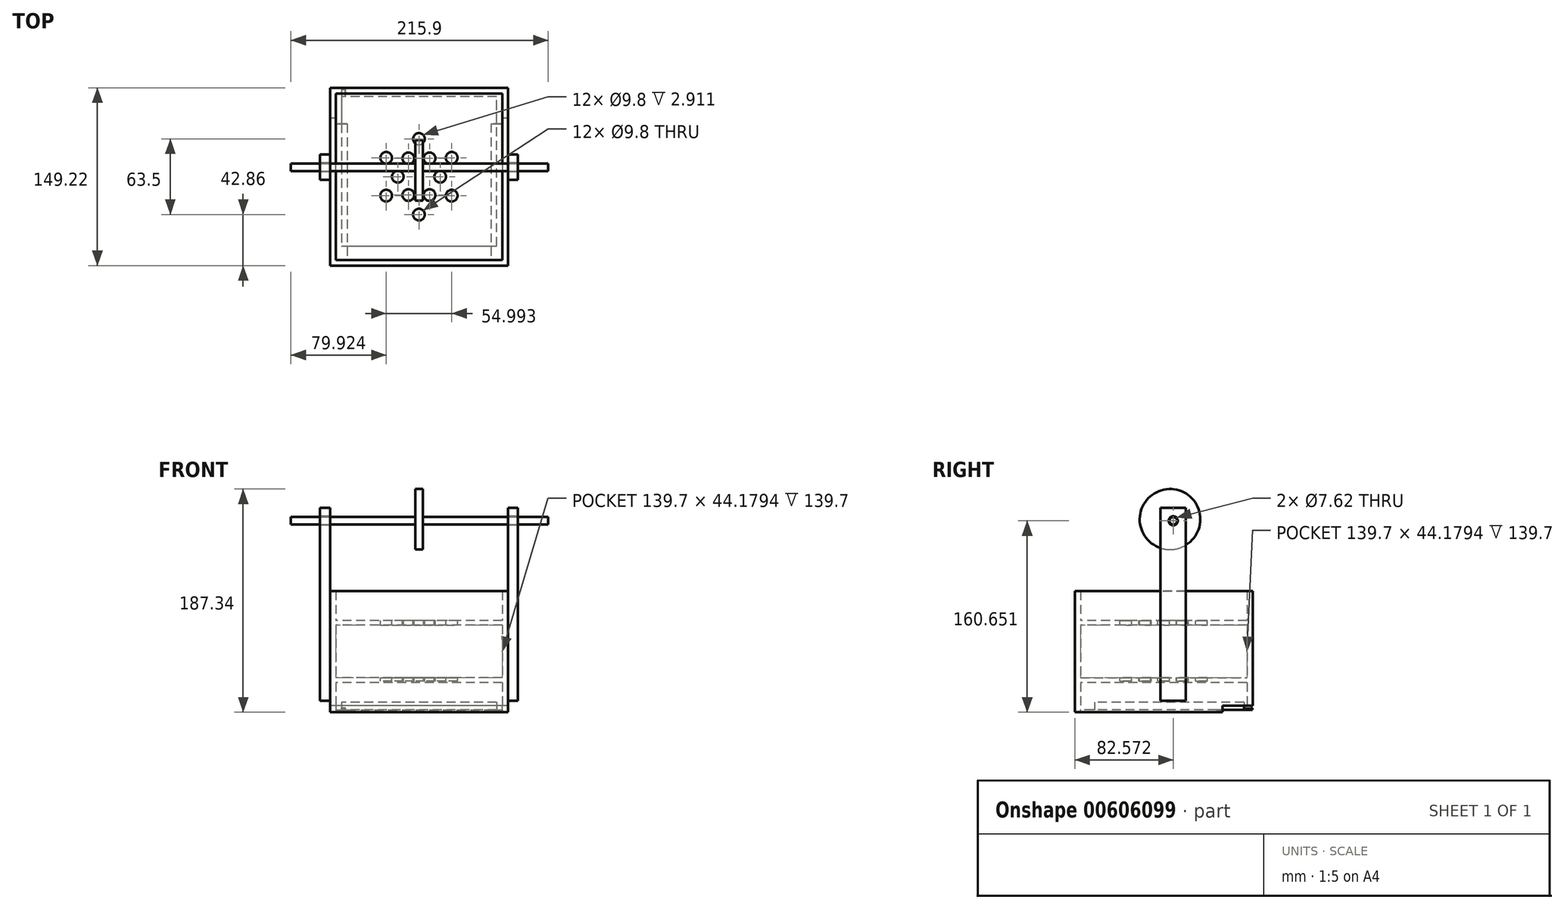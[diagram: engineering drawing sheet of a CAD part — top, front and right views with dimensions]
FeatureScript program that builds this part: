
annotation { "Feature Type Name" : "Feature", "Feature Type Description" : "" }
export const myFeature = defineFeature(function(context is Context, id is Id, definition is map)
    precondition{}
    {
        {
            var Q0;
            Q0=qCreatedBy(makeId("Top.planeOp"),FACE);
            var sketch = newSketch(context, id + "F0", { "sketchPlane" : qUnion([Q0])});
            skLineSegment(sketch, "E0", {"start": v(0, 139.7) * mm, "end": v(139.7, 139.7) * mm});
            skLineSegment(sketch, "E1", {"start": v(139.7, 139.7) * mm, "end": v(139.7, 0) * mm});
            skLineSegment(sketch, "E2", {"start": v(139.7, 0) * mm, "end": v(0, 0) * mm});
            skLineSegment(sketch, "E3", {"start": v(0, 0) * mm, "end": v(0, 139.7) * mm});
            skLineSegment(sketch, "E4", {"start": v(139.7, 95.25) * mm, "end": v(139.7, 69.85) * mm});
            skLineSegment(sketch, "E5", {"start": v(120.65, 19.05) * mm, "end": v(120.65, 120.65) * mm});
            skLineSegment(sketch, "E6", {"start": v(120.65, 120.65) * mm, "end": v(19.05, 120.65) * mm});
            skLineSegment(sketch, "E7", {"start": v(19.05, 120.65) * mm, "end": v(19.05, 19.05) * mm});
            skLineSegment(sketch, "E8", {"start": v(19.05, 19.05) * mm, "end": v(120.65, 19.05) * mm});
            skCircle(sketch, "E9", {"center": v(70, 69.85) * mm, "radius": 45.29 * mm});
            skLineSegment(sketch, "E10", {"start": v(-4.76, 139.7) * mm, "end": v(-4.76, 0) * mm});
            skLineSegment(sketch, "E11", {"start": v(140.6, -4.76) * mm, "end": v(0, -4.76) * mm});
            skLineSegment(sketch, "E12", {"start": v(0, -4.76) * mm, "end": v(-4.76, -4.76) * mm});
            skLineSegment(sketch, "E13", {"start": v(-4.76, -4.76) * mm, "end": v(-4.76, 0) * mm});
            skLineSegment(sketch, "E14", {"start": v(140.6, 144.46) * mm, "end": v(-4.76, 144.46) * mm});
            skLineSegment(sketch, "E15", {"start": v(-4.76, 144.46) * mm, "end": v(-4.76, 139.7) * mm});
            skLineSegment(sketch, "E16", {"start": v(140.6, -4.76) * mm, "end": v(144.46, -4.76) * mm});
            skLineSegment(sketch, "E17", {"start": v(144.46, -4.76) * mm, "end": v(144.46, 144.46) * mm});
            skLineSegment(sketch, "E18", {"start": v(144.46, 144.46) * mm, "end": v(140.6, 144.46) * mm});
            skLineSegment(sketch, "E19", {"start": v(-4.76, 88.47) * mm, "end": v(-13.23, 88.47) * mm});
            skLineSegment(sketch, "E20", {"start": v(-13.23, 88.47) * mm, "end": v(-13.23, 67.15) * mm});
            skLineSegment(sketch, "E21", {"start": v(-13.23, 67.15) * mm, "end": v(-4.76, 67.15) * mm});
            skLineSegment(sketch, "E22", {"start": v(144.46, 88.47) * mm, "end": v(152.93, 88.47) * mm});
            skLineSegment(sketch, "E23", {"start": v(152.93, 88.47) * mm, "end": v(152.93, 73.37) * mm});
            skLineSegment(sketch, "E24", {"start": v(152.93, 73.37) * mm, "end": v(152.93, 67.15) * mm});
            skLineSegment(sketch, "E25", {"start": v(152.93, 67.15) * mm, "end": v(144.46, 67.15) * mm});
            skSolve(sketch);
        }
        {
            var Q0;
            {var subQ1=sQuery(id+"F0.wireOp",EDGE,"E0");Q0=makeQuery(id+"F0.imprint","IMPRINT",FACE,{"disambiguationData":[TD([[makeQuery(id+"F0.imprint","IMPRINT",EDGE,{"derivedFrom":subQ1}),1.0]])]});}
            extrude(context, id + "F1", {"entities" : qUnion([Q0]), "depth" : 101.6 * mm, "offsetDistance" : 25.4 * mm});
        }
        {
            var Q0;
            {var subQ0=sQuery(id+"F0.wireOp",EDGE,"E22");Q0=makeQuery(id+"F0.imprint","IMPRINT",FACE,{"disambiguationData":[TD([[makeQuery(id+"F0.imprint","IMPRINT",EDGE,{"derivedFrom":subQ0}),-1.0]])]});}
            var Q1;
            {var subQ0=sQuery(id+"F0.wireOp",EDGE,"E19");Q1=makeQuery(id+"F0.imprint","IMPRINT",FACE,{"disambiguationData":[TD([[makeQuery(id+"F0.imprint","IMPRINT",EDGE,{"derivedFrom":subQ0}),1.0]])]});}
            extrude(context, id + "F2", {"entities" : qUnion([Q0, Q1]), "operationType" : NewBodyOperationType.ADD, "depth" : 171.45 * mm, "offsetDistance" : 25.4 * mm});
        }
        {
            var Q0;
            Q0=makeQuery(id+"F2.opExtrude","SWEPT_FACE",FACE,{"disambiguationData":[OSD([sQuery(id+"F0.wireOp",EDGE,"E20")])]});
            var sketch = newSketch(context, id + "F3", { "sketchPlane" : qUnion([Q0])});
            skLineSegment(sketch, "E26", {"start": v(-88.47, 9.53) * mm, "end": v(-67.15, 9.53) * mm});
            skSolve(sketch);
        }
        {
            var Q0;
            Q0 = qSketchRegion(id + "F3", true);
            var Q1;
            {var subQ0=sQuery(id+"F3.wireOp",EDGE,"E26");Q1=makeQuery(id+"F3.imprint","IMPRINT",FACE,{"disambiguationData":[TD([[makeQuery(id+"F3.imprint","IMPRINT",EDGE,{"derivedFrom":subQ0}),-1.0]])]});}
            extrude(context, id + "F4", {"entities" : qUnion([Q0, Q1]), "operationType" : NewBodyOperationType.REMOVE, "oppositeDirection" : true, "depth" : 8.47 * mm, "offsetDistance" : 25.4 * mm});
        }
        {
            var Q0;
            Q0=makeQuery(id+"F2.opExtrude","SWEPT_FACE",FACE,{"disambiguationData":[OSD([sQuery(id+"F0.wireOp",EDGE,"E23"),sQuery(id+"F0.wireOp",EDGE,"E24")])]});
            var sketch = newSketch(context, id + "F5", { "sketchPlane" : qUnion([Q0])});
            skLineSegment(sketch, "E27", {"start": v(67.15, 0) * mm, "end": v(67.15, 9.53) * mm});
            skLineSegment(sketch, "E28", {"start": v(67.15, 9.53) * mm, "end": v(88.47, 9.53) * mm});
            skLineSegment(sketch, "E29", {"start": v(88.47, 9.53) * mm, "end": v(88.47, 0) * mm});
            skSolve(sketch);
        }
        {
            var Q0;
            Q0 = qSketchRegion(id + "F5", true);
            var Q1;
            Q1=makeQuery(id+"F5.imprint","IMPRINT",FACE,{"disambiguationData":[TD([[makeQuery(id+"F5.imprint","IMPRINT",EDGE,{"derivedFrom":sQuery(id+"F5.wireOp",EDGE,"E27")}),1.0]])]});
            extrude(context, id + "F6", {"entities" : qUnion([Q0, Q1]), "operationType" : NewBodyOperationType.REMOVE, "oppositeDirection" : true, "depth" : 8.47 * mm, "offsetDistance" : 25.4 * mm});
        }
        {
            var Q0;
            Q0=makeQuery(id+"F2.opExtrude","SWEPT_FACE",FACE,{"disambiguationData":[OSD([sQuery(id+"F0.wireOp",EDGE,"E20")])]});
            var sketch = newSketch(context, id + "F7", { "sketchPlane" : qUnion([Q0])});
            skLineSegment(sketch, "E30", {"start": v(-77.81, 171.45) * mm, "end": v(-77.81, 160.65) * mm});
            skCircle(sketch, "E31", {"center": v(-77.81, 160.65) * mm, "radius": 3.81 * mm});
            skSolve(sketch);
        }
        {
            var Q0;
            Q0=makeQuery(id+"F7.imprint","IMPRINT",FACE,{"disambiguationData":[TD([[makeQuery(id+"F7.imprint","IMPRINT",EDGE,{"derivedFrom":sQuery(id+"F7.wireOp",EDGE,"E31")}),1.0]])]});
            extrude(context, id + "F8", {"entities" : qUnion([Q0]), "operationType" : NewBodyOperationType.REMOVE, "oppositeDirection" : true, "depth" : 177.8 * mm, "offsetDistance" : 25.4 * mm});
        }
        {
            var Q0;
            Q0=makeQuery(id+"F1.opExtrude","SWEPT_FACE",FACE,{"disambiguationData":[OSD([sQuery(id+"F0.wireOp",EDGE,"E2")])]});
            var sketch = newSketch(context, id + "F9", { "sketchPlane" : qUnion([Q0])});
            skLineSegment(sketch, "E32", {"start": v(0, 0) * mm, "end": v(0, 2.12) * mm});
            skLineSegment(sketch, "E33", {"start": v(0, 2.12) * mm, "end": v(-9.52, 2.12) * mm});
            skLineSegment(sketch, "E34", {"start": v(-9.52, 2.12) * mm, "end": v(-9.52, 0) * mm});
            skLineSegment(sketch, "E35", {"start": v(-139.7, 0) * mm, "end": v(-130.18, 0) * mm});
            skLineSegment(sketch, "E36", {"start": v(-130.18, 0) * mm, "end": v(-130.18, 2.12) * mm});
            skLineSegment(sketch, "E37", {"start": v(-130.18, 2.12) * mm, "end": v(-139.7, 2.12) * mm});
            skLineSegment(sketch, "E38", {"start": v(-139.7, 2.12) * mm, "end": v(-139.7, 0) * mm});
            skSolve(sketch);
        }
        {
            var Q0;
            Q0 = qSketchRegion(id + "F9", true);
            var Q1;
            {var subQ0=sQuery(id+"F9.wireOp",EDGE,"E32");Q1=makeQuery(id+"F9.imprint","IMPRINT",FACE,{"disambiguationData":[TD([[makeQuery(id+"F9.imprint","IMPRINT",EDGE,{"derivedFrom":subQ0}),-1.0]])]});}
            extrude(context, id + "F10", {"entities" : qUnion([Q0, Q1]), "operationType" : NewBodyOperationType.ADD, "depth" : 114.3 * mm, "offsetDistance" : 25.4 * mm});
        }
        {
            var Q0;
            Q0=makeQuery(id+"F1.opExtrude","SWEPT_FACE",FACE,{"disambiguationData":[OSD([sQuery(id+"F0.wireOp",EDGE,"E14"),sQuery(id+"F0.wireOp",EDGE,"E18")])]});
            var sketch = newSketch(context, id + "F11", { "sketchPlane" : qUnion([Q0])});
            skLineSegment(sketch, "E39", {"start": v(-144.46, 0) * mm, "end": v(-144.46, 5.6) * mm});
            skLineSegment(sketch, "E40", {"start": v(-144.46, 5.6) * mm, "end": v(4.76, 5.6) * mm});
            skLineSegment(sketch, "E41", {"start": v(4.76, 5.6) * mm, "end": v(4.76, 0) * mm});
            skLineSegment(sketch, "E42", {"start": v(4.76, 0) * mm, "end": v(-144.46, 0) * mm});
            skSolve(sketch);
        }
        {
            var Q0;
            Q0=makeQuery(id+"F11.imprint","IMPRINT",FACE,{"disambiguationData":[TD([[makeQuery(id+"F11.imprint","IMPRINT",EDGE,{"derivedFrom":sQuery(id+"F11.wireOp",EDGE,"E39")}),1.0]])]});
            extrude(context, id + "F12", {"entities" : qUnion([Q0]), "operationType" : NewBodyOperationType.REMOVE, "oppositeDirection" : true, "depth" : 25.4 * mm, "offsetDistance" : 25.4 * mm});
        }
        {
            var Q0;
            Q0=makeQuery(id+"F10.opExtrude","SWEPT_FACE",FACE,{"disambiguationData":[OSD([sQuery(id+"F9.wireOp",EDGE,"E33")])]});
            var sketch = newSketch(context, id + "F13", { "sketchPlane" : qUnion([Q0])});
            skLineSegment(sketch, "E43", {"start": v(4.76, 114.3) * mm, "end": v(4.76, 11.8) * mm});
            skLineSegment(sketch, "E44", {"start": v(4.76, 11.8) * mm, "end": v(135.03, 11.8) * mm});
            skLineSegment(sketch, "E45", {"start": v(135.03, 11.8) * mm, "end": v(135.03, 137.06) * mm});
            skLineSegment(sketch, "E46", {"start": v(135.03, 137.06) * mm, "end": v(4.76, 137.06) * mm});
            skLineSegment(sketch, "E47", {"start": v(4.76, 137.06) * mm, "end": v(4.76, 114.3) * mm});
            skSolve(sketch);
        }
        {
            var Q0;
            {var subQ0=sQuery(id+"F13.wireOp",EDGE,"E43");Q0=makeQuery(id+"F13.imprint","IMPRINT",FACE,{"disambiguationData":[TD([[makeQuery(id+"F13.imprint","IMPRINT",EDGE,{"derivedFrom":subQ0}),1.0]])]});}
            var Q1;
            {var subQ1=sQuery(id+"F13.wireOp",EDGE,"E45");Q1=makeQuery(id+"F13.imprint","IMPRINT",FACE,{"disambiguationData":[TD([[makeQuery(id+"F13.imprint","IMPRINT",EDGE,{"derivedFrom":subQ1}),1.0]])]});}
            extrude(context, id + "F14", {"entities" : qUnion([Q0, Q1]), "operationType" : NewBodyOperationType.ADD, "depth" : 6.35 * mm, "offsetDistance" : 25.4 * mm});
        }
        {
            var Q0;
            Q0=makeQuery(id+"F1.opExtrude","SWEPT_FACE",FACE,{"disambiguationData":[OSD([sQuery(id+"F0.wireOp",EDGE,"E3")])]});
            var sketch = newSketch(context, id + "F15", { "sketchPlane" : qUnion([Q0])});
            skLineSegment(sketch, "E48", {"start": v(0, 28.92) * mm, "end": v(139.7, 28.92) * mm});
            skLineSegment(sketch, "E49", {"start": v(139.7, 28.92) * mm, "end": v(139.7, 73.1) * mm});
            skLineSegment(sketch, "E50", {"start": v(139.7, 73.1) * mm, "end": v(0, 73.1) * mm});
            skLineSegment(sketch, "E51", {"start": v(139.7, 28.92) * mm, "end": v(139.7, 24.87) * mm});
            skLineSegment(sketch, "E52", {"start": v(139.7, 24.87) * mm, "end": v(0, 24.87) * mm});
            skLineSegment(sketch, "E53", {"start": v(139.7, 73.1) * mm, "end": v(139.7, 76.8) * mm});
            skLineSegment(sketch, "E54", {"start": v(139.7, 76.8) * mm, "end": v(0, 76.8) * mm});
            skSolve(sketch);
        }
        {
            var Q0;
            Q0 = qSketchRegion(id + "F15", true);
            var Q1;
            {var subQ0=sQuery(id+"F15.wireOp",EDGE,"E50");Q1=makeQuery(id+"F15.imprint","IMPRINT",FACE,{"disambiguationData":[TD([[makeQuery(id+"F15.imprint","IMPRINT",EDGE,{"derivedFrom":subQ0}),-1.0]])]});}
            var Q2;
            {var subQ0=sQuery(id+"F15.wireOp",EDGE,"E48");Q2=makeQuery(id+"F15.imprint","IMPRINT",FACE,{"disambiguationData":[TD([[makeQuery(id+"F15.imprint","IMPRINT",EDGE,{"derivedFrom":subQ0}),-1.0]])]});}
            extrude(context, id + "F16", {"entities" : qUnion([Q0, Q1, Q2]), "operationType" : NewBodyOperationType.ADD, "depth" : 139.7 * mm, "offsetDistance" : 25.4 * mm});
        }
        {
            var Q0;
            Q0=makeQuery(id+"F16.opExtrude","SWEPT_FACE",FACE,{"disambiguationData":[OSD([sQuery(id+"F15.wireOp",EDGE,"E54")])]});
            var sketch = newSketch(context, id + "F17", { "sketchPlane" : qUnion([Q0])});
            skLineSegment(sketch, "E55", {"start": v(139.7, 0) * mm, "end": v(139.7, 139.7) * mm});
            skPoint(sketch, "E56", {"position": v(69.85, 69.85) * mm});
            skCircle(sketch, "E57", {"center": v(87.63, 69.85) * mm, "radius": 4.9 * mm});
            skCircle(sketch, "E58.1.0", {"center": v(78.74, 85.25) * mm, "radius": 4.9 * mm});
            skCircle(sketch, "E58.2.0", {"center": v(60.96, 85.25) * mm, "radius": 4.9 * mm});
            skCircle(sketch, "E58.3.0", {"center": v(52.07, 69.85) * mm, "radius": 4.9 * mm});
            skCircle(sketch, "E58.4.0", {"center": v(60.96, 54.45) * mm, "radius": 4.9 * mm});
            skCircle(sketch, "E58.5.0", {"center": v(78.74, 54.45) * mm, "radius": 4.9 * mm});
            skCircle(sketch, "E59", {"center": v(69.85, 101.6) * mm, "radius": 4.9 * mm});
            skCircle(sketch, "E60.1.0", {"center": v(42.35, 85.73) * mm, "radius": 4.9 * mm});
            skCircle(sketch, "E60.2.0", {"center": v(42.35, 53.98) * mm, "radius": 4.9 * mm});
            skCircle(sketch, "E60.3.0", {"center": v(69.85, 38.1) * mm, "radius": 4.9 * mm});
            skCircle(sketch, "E60.4.0", {"center": v(97.35, 53.97) * mm, "radius": 4.9 * mm});
            skCircle(sketch, "E60.5.0", {"center": v(97.35, 85.73) * mm, "radius": 4.9 * mm});
            skSolve(sketch);
        }
        {
            var Q0;
            Q0 = qSketchRegion(id + "F15", true);
            var Q1;
            Q1 = qSketchRegion(id + "F17", true);
            extrude(context, id + "F18", {"entities" : qUnion([Q0, Q1]), "operationType" : NewBodyOperationType.REMOVE, "depth" : 25.4 * mm, "offsetDistance" : 25.4 * mm});
        }
        {
            var Q0;
            Q0 = qSketchRegion(id + "F17", true);
            extrude(context, id + "F19", {"entities" : qUnion([Q0]), "operationType" : NewBodyOperationType.REMOVE, "oppositeDirection" : true, "depth" : 50.8 * mm, "offsetDistance" : 25.4 * mm});
        }
        {
            var Q0;
            Q0=makeQuery(id+"F2.opExtrude","SWEPT_FACE",FACE,{"disambiguationData":[OSD([sQuery(id+"F0.wireOp",EDGE,"E23"),sQuery(id+"F0.wireOp",EDGE,"E24")])]});
            var sketch = newSketch(context, id + "F20", { "sketchPlane" : qUnion([Q0])});
            skCircle(sketch, "E61", {"center": v(77.81, 160.65) * mm, "radius": 3.18 * mm});
            skSolve(sketch);
        }
        {
            var Q0;
            Q0=makeQuery(id+"F20.imprint","IMPRINT",FACE,{"disambiguationData":[TD([[makeQuery(id+"F20.imprint","IMPRINT",EDGE,{"derivedFrom":sQuery(id+"F20.wireOp",EDGE,"E61")}),1.0]])]});
            extrude(context, id + "F21", {"entities" : qUnion([Q0]), "oppositeDirection" : true, "depth" : 177.8 * mm, "offsetDistance" : 25.4 * mm});
        }
        {
            var Q0;
            Q0=makeQuery(id+"F21.opExtrude","CAP_FACE",FACE,{"disambiguationData":[OSD([sQuery(id+"F20.wireOp",EDGE,"E61")])],"isStart":true});
            extrude(context, id + "F22", {"entities" : qUnion([Q0]), "operationType" : NewBodyOperationType.ADD, "depth" : 25.4 * mm, "offsetDistance" : 25.4 * mm});
        }
        {
            var Q0;
            Q0=makeQuery(id+"F21.opExtrude","CAP_FACE",FACE,{"disambiguationData":[OSD([sQuery(id+"F20.wireOp",EDGE,"E61")])],"isStart":false});
            extrude(context, id + "F23", {"entities" : qUnion([Q0]), "operationType" : NewBodyOperationType.ADD, "depth" : 12.7 * mm, "offsetDistance" : 25.4 * mm});
        }
        {
            var Q0;
            Q0=makeQuery(id+"F1.opExtrude","CAP_EDGE",EDGE,{"disambiguationData":[OSD([sQuery(id+"F0.wireOp",EDGE,"E14"),sQuery(id+"F0.wireOp",EDGE,"E18")])],"isStart":false});
            cPoint(context, id + "F24", {"entities" : qUnion([Q0]), "parameter" : 0.5});
        }
        {
            var Q0;
            Q0=qCreatedBy(makeId("Right.planeOp"),FACE);
            var Q1;
            Q1 = qCreatedBy(id + "F24" ,VERTEX);
            cPlane(context, id + "F25", {"entities" : qUnion([Q0, Q1]), "cplaneType" : CPlaneType.PLANE_POINT, "offset" : 25.4 * mm, "width" : 152.4 * mm, "height" : 152.4 * mm});
        }
        {
            var Q0;
            Q0=qCreatedBy(id+"F25.planeOp",FACE);
            var sketch = newSketch(context, id + "F26", { "sketchPlane" : qUnion([Q0])});
            skCircle(sketch, "E62", {"center": v(75.1, 161.94) * mm, "radius": 25.4 * mm});
            skSolve(sketch);
        }
        {
            var Q0;
            Q0 = qSketchRegion(id + "F26", true);
            extrude(context, id + "F27", {"entities" : qUnion([Q0]), "operationType" : NewBodyOperationType.ADD, "depth" : 3.17 * mm, "offsetDistance" : 25.4 * mm});
        }
        {
            var Q0;
            Q0=makeQuery(id+"F27.opExtrude","CAP_FACE",FACE,{"disambiguationData":[OSD([sQuery(id+"F26.wireOp",EDGE,"E62")])],"isStart":true});
            extrude(context, id + "F28", {"entities" : qUnion([Q0]), "operationType" : NewBodyOperationType.ADD, "depth" : 3.17 * mm, "offsetDistance" : 25.4 * mm});
        }
        {
            var Q0;
            Q0=makeQuery(id+"F14.opExtrude","SWEPT_FACE",FACE,{"disambiguationData":[OSD([sQuery(id+"F13.wireOp",EDGE,"E43"),sQuery(id+"F13.wireOp",EDGE,"E47")])]});
            var sketch = newSketch(context, id + "F29", { "sketchPlane" : qUnion([Q0])});
            skLineSegment(sketch, "E63", {"start": v(-137.06, 2.12) * mm, "end": v(-144.05, 2.12) * mm});
            skLineSegment(sketch, "E64", {"start": v(-144.05, 2.12) * mm, "end": v(-144.05, 3.5) * mm});
            skLineSegment(sketch, "E65", {"start": v(-144.05, 3.5) * mm, "end": v(-142.9, 3.5) * mm});
            skLineSegment(sketch, "E66", {"start": v(-142.9, 3.5) * mm, "end": v(-142.9, 2.85) * mm});
            skLineSegment(sketch, "E67", {"start": v(-142.9, 2.85) * mm, "end": v(-143.45, 2.85) * mm});
            skLineSegment(sketch, "E68", {"start": v(-143.45, 2.85) * mm, "end": v(-137.06, 2.85) * mm});
            skSolve(sketch);
        }
        {
            var Q0;
            Q0 = qSketchRegion(id + "F29", true);
            var Q1;
            {var subQ1=sQuery(id+"F29.wireOp",EDGE,"E63");Q1=makeQuery(id+"F29.imprint","IMPRINT",FACE,{"disambiguationData":[TD([[makeQuery(id+"F29.imprint","IMPRINT",EDGE,{"derivedFrom":subQ1}),-1.0]])]});}
            extrude(context, id + "F30", {"entities" : qUnion([Q0, Q1]), "operationType" : NewBodyOperationType.ADD, "oppositeDirection" : true, "depth" : 3.17 * mm, "offsetDistance" : 25.4 * mm});
        }
    });
